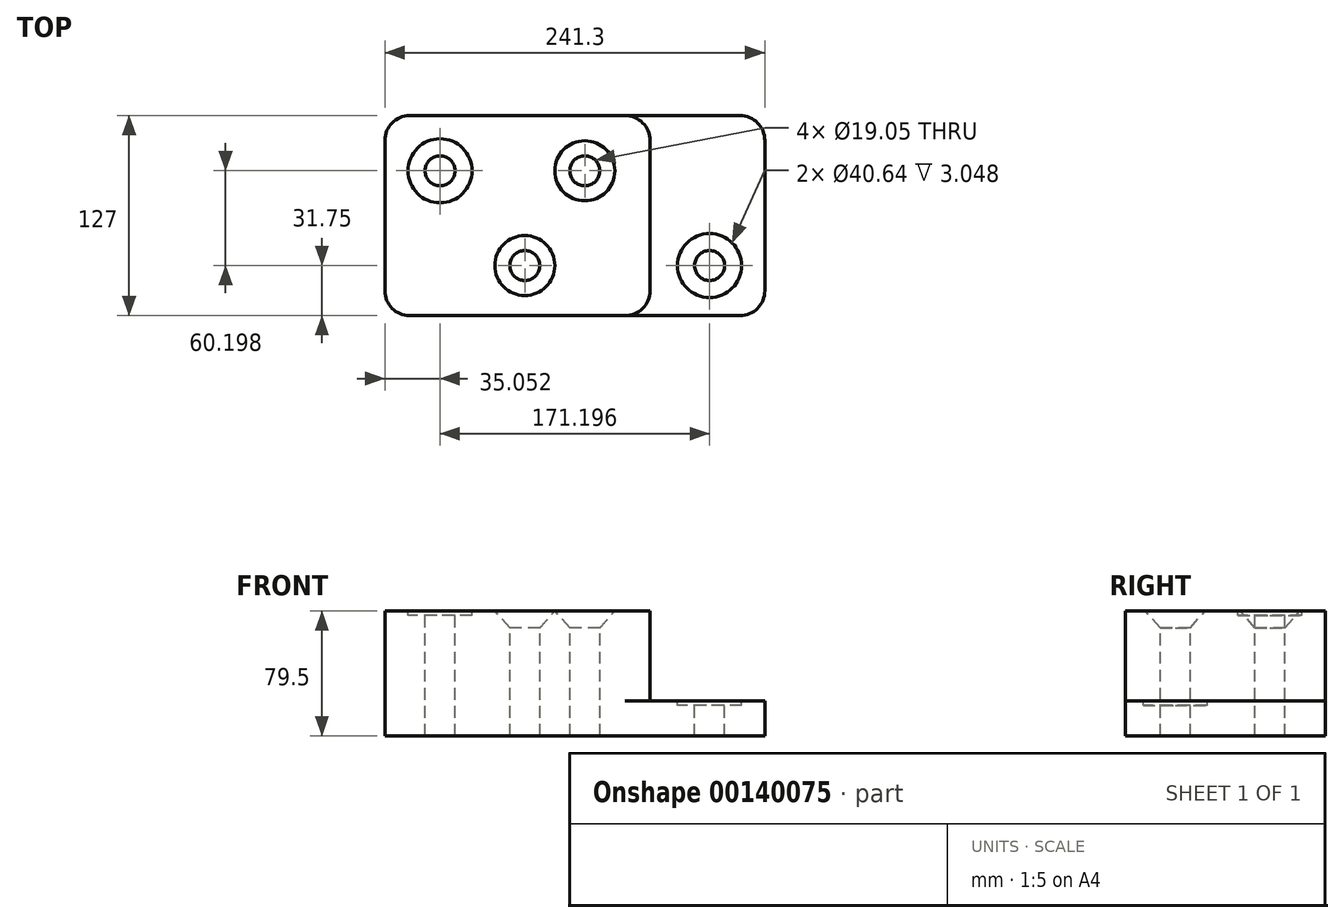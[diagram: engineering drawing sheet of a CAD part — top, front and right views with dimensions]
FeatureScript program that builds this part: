
annotation { "Feature Type Name" : "Feature", "Feature Type Description" : "" }
export const myFeature = defineFeature(function(context is Context, id is Id, definition is map)
    precondition{}
    {
        {
            var Q0;
            Q0=qCreatedBy(makeId("Top.planeOp"),FACE);
            var sketch = newSketch(context, id + "F0", { "sketchPlane" : qUnion([Q0])});
            skLineSegment(sketch, "E0.bottom", {"start": v(0, 0) * mm, "end": v(168.4, 0) * mm});
            skLineSegment(sketch, "E0.top", {"start": v(0, 127) * mm, "end": v(168.4, 127) * mm});
            skLineSegment(sketch, "E0.left", {"start": v(0, 0) * mm, "end": v(0, 127) * mm});
            skLineSegment(sketch, "E0.right", {"start": v(168.4, 0) * mm, "end": v(168.4, 127) * mm});
            skLineSegment(sketch, "E1.bottom", {"start": v(168.4, 127) * mm, "end": v(241.3, 127) * mm});
            skLineSegment(sketch, "E1.top", {"start": v(168.4, 0) * mm, "end": v(241.3, 0) * mm});
            skLineSegment(sketch, "E1.left", {"start": v(168.4, 127) * mm, "end": v(168.4, 0) * mm});
            skLineSegment(sketch, "E1.right", {"start": v(241.3, 127) * mm, "end": v(241.3, 0) * mm});
            skSolve(sketch);
        }
        {
            var Q0;
            Q0=makeQuery(id+"F0.imprint","IMPRINT",FACE,{"disambiguationData":[TD([[makeQuery(id+"F0.imprint","IMPRINT",EDGE,{"derivedFrom":sQuery(id+"F0.wireOp",EDGE,"E0.bottom")}),1.0]])]});
            extrude(context, id + "F1", {"entities" : qUnion([Q0]), "depth" : 79.5 * mm});
        }
        {
            var Q0;
            Q0=makeQuery(id+"F1.opExtrude","SWEPT_EDGE",EDGE,{"disambiguationData":[OSD([sQuery(id+"F0.wireOp",EDGE,"E0.bottom"),sQuery(id+"F0.wireOp",EDGE,"E1.top"),sQuery(id+"F0.wireOp",EDGE,"E1.left")])]});
            var Q1;
            Q1=makeQuery(id+"F1.opExtrude","SWEPT_EDGE",EDGE,{"disambiguationData":[OSD([sQuery(id+"F0.wireOp",EDGE,"E0.top"),sQuery(id+"F0.wireOp",EDGE,"E1.bottom"),sQuery(id+"F0.wireOp",EDGE,"E1.left")])]});
            var Q2;
            Q2=makeQuery(id+"F1.opExtrude","SWEPT_EDGE",EDGE,{"disambiguationData":[OSD([sQuery(id+"F0.wireOp",EDGE,"E0.bottom"),sQuery(id+"F0.wireOp",EDGE,"E0.left")])]});
            var Q3;
            Q3=makeQuery(id+"F1.opExtrude","SWEPT_EDGE",EDGE,{"disambiguationData":[OSD([sQuery(id+"F0.wireOp",EDGE,"E0.top"),sQuery(id+"F0.wireOp",EDGE,"E0.left")])]});
            fillet(context, id + "F2", {"entities" : qUnion([Q0, Q1, Q2, Q3]), "radius" : 15.75 * mm, "tangentPropagation" : true, "allowEdgeOverflow" : false});
        }
        {
            var Q0;
            Q0=qCreatedBy(makeId("Top.planeOp"),FACE);
            var sketch = newSketch(context, id + "F3", { "sketchPlane" : qUnion([Q0])});
            skArc(sketch, "E2.0", {"start": v(152.65, 0) * mm, "mid": v(163.79, 4.61) * mm, "end": v(168.4, 15.75) * mm});
            skLineSegment(sketch, "E3.0", {"start": v(168.4, 111.25) * mm, "end": v(168.4, 15.75) * mm});
            skArc(sketch, "E4.0", {"start": v(168.4, 111.25) * mm, "mid": v(163.79, 122.39) * mm, "end": v(152.65, 127) * mm});
            skLineSegment(sketch, "E5.0", {"start": v(168.4, 127) * mm, "end": v(241.3, 127) * mm});
            skLineSegment(sketch, "E6.0", {"start": v(241.3, 127) * mm, "end": v(241.3, 0) * mm});
            skLineSegment(sketch, "E7.0", {"start": v(168.4, 0) * mm, "end": v(241.3, 0) * mm});
            skLineSegment(sketch, "E8", {"start": v(168.4, 0) * mm, "end": v(152.65, 0) * mm});
            skLineSegment(sketch, "E9", {"start": v(152.65, 127) * mm, "end": v(168.4, 127) * mm});
            skSolve(sketch);
        }
        {
            var Q0;
            Q0 = qSketchRegion(id + "F3", true);
            extrude(context, id + "F4", {"entities" : qUnion([Q0]), "operationType" : NewBodyOperationType.ADD, "depth" : 22.35 * mm});
        }
        {
            var Q0;
            Q0=makeQuery(id+"F4.opExtrude","SWEPT_EDGE",EDGE,{"disambiguationData":[OSD([sQuery(id+"F3.wireOp",EDGE,"E6.0"),sQuery(id+"F3.wireOp",EDGE,"E7.0")])]});
            var Q1;
            Q1=makeQuery(id+"F4.opExtrude","SWEPT_EDGE",EDGE,{"disambiguationData":[OSD([sQuery(id+"F3.wireOp",EDGE,"E5.0"),sQuery(id+"F3.wireOp",EDGE,"E6.0")])]});
            fillet(context, id + "F5", {"entities" : qUnion([Q0, Q1]), "radius" : 15.75 * mm, "tangentPropagation" : true, "allowEdgeOverflow" : false});
        }
        {
            var Q0;
            Q0=makeQuery(id+"F1.opExtrude","CAP_FACE",FACE,{"disambiguationData":[OSD([sQuery(id+"F0.wireOp",EDGE,"E0.bottom"),sQuery(id+"F0.wireOp",EDGE,"E0.top"),sQuery(id+"F0.wireOp",EDGE,"E0.left"),sQuery(id+"F0.wireOp",EDGE,"E1.left")])],"isStart":false});
            var sketch = newSketch(context, id + "F6", { "sketchPlane" : qUnion([Q0])});
            skPoint(sketch, "E10", {"position": v(88.9, 31.75) * mm});
            skPoint(sketch, "E11", {"position": v(35.05, 91.95) * mm});
            skPoint(sketch, "E12", {"position": v(127, 91.95) * mm});
            skPoint(sketch, "E13", {"position": v(206.25, 31.75) * mm});
            skSolve(sketch);
        }
        {
            var Q0;
            Q0=sQuery(id+"F6.wireOp",VERTEX,"E10");
            var Q1;
            Q1=sQuery(id+"F6.wireOp",VERTEX,"E12");
            var Q2;
            Q2=makeQuery(id+"F1.opExtrude","SWEPT_BODY",BODY,{"disambiguationData":[OSD([sQuery(id+"F0.wireOp",EDGE,"E0.bottom"),sQuery(id+"F0.wireOp",EDGE,"E0.top"),sQuery(id+"F0.wireOp",EDGE,"E0.left"),sQuery(id+"F0.wireOp",EDGE,"E1.left")])]});
            hole(context, id + "F7", {"style" : HoleStyle.C_SINK, "endStyle" : HoleEndStyle.THROUGH, "holeDiameter" : 19.05 * mm, "cSinkDiameter" : 38.1 * mm, "cSinkAngle" : 82 * degree, "locations" : qUnion([Q0, Q1]), "scope" : qUnion([Q2]), "isTappedThrough" : true});
        }
        {
            var Q0;
            Q0=sQuery(id+"F6.wireOp",VERTEX,"E11");
            var Q1;
            Q1=makeQuery(id+"F1.opExtrude","SWEPT_BODY",BODY,{"disambiguationData":[OSD([sQuery(id+"F0.wireOp",EDGE,"E0.bottom"),sQuery(id+"F0.wireOp",EDGE,"E0.top"),sQuery(id+"F0.wireOp",EDGE,"E0.left"),sQuery(id+"F0.wireOp",EDGE,"E1.left")])]});
            hole(context, id + "F8", {"style" : HoleStyle.C_BORE, "endStyle" : HoleEndStyle.THROUGH, "holeDiameter" : 19.05 * mm, "cBoreDiameter" : 40.64 * mm, "cBoreDepth" : 3.05 * mm, "locations" : qUnion([Q0]), "scope" : qUnion([Q1]), "isTappedThrough" : true});
        }
        {
            var Q0;
            Q0=makeQuery(id+"F4.opExtrude","CAP_FACE",FACE,{"disambiguationData":[OSD([sQuery(id+"F3.wireOp",EDGE,"E2.0"),sQuery(id+"F3.wireOp",EDGE,"E3.0"),sQuery(id+"F3.wireOp",EDGE,"E4.0"),sQuery(id+"F3.wireOp",EDGE,"E5.0"),sQuery(id+"F3.wireOp",EDGE,"E6.0"),sQuery(id+"F3.wireOp",EDGE,"E7.0"),sQuery(id+"F3.wireOp",EDGE,"E8"),sQuery(id+"F3.wireOp",EDGE,"E9")])],"isStart":false});
            var sketch = newSketch(context, id + "F9", { "sketchPlane" : qUnion([Q0])});
            skPoint(sketch, "E14.0", {"position": v(206.25, 31.75) * mm});
            skSolve(sketch);
        }
        {
            var Q0;
            Q0=sQuery(id+"F9.wireOp",VERTEX,"E14.0");
            var Q1;
            Q1=makeQuery(id+"F1.opExtrude","SWEPT_BODY",BODY,{"disambiguationData":[OSD([sQuery(id+"F0.wireOp",EDGE,"E0.bottom"),sQuery(id+"F0.wireOp",EDGE,"E0.top"),sQuery(id+"F0.wireOp",EDGE,"E0.left"),sQuery(id+"F0.wireOp",EDGE,"E1.left")])]});
            hole(context, id + "F10", {"style" : HoleStyle.C_BORE, "endStyle" : HoleEndStyle.THROUGH, "holeDiameter" : 19.05 * mm, "cBoreDiameter" : 40.64 * mm, "cBoreDepth" : 3.05 * mm, "locations" : qUnion([Q0]), "scope" : qUnion([Q1]), "isTappedThrough" : true});
        }
    });
